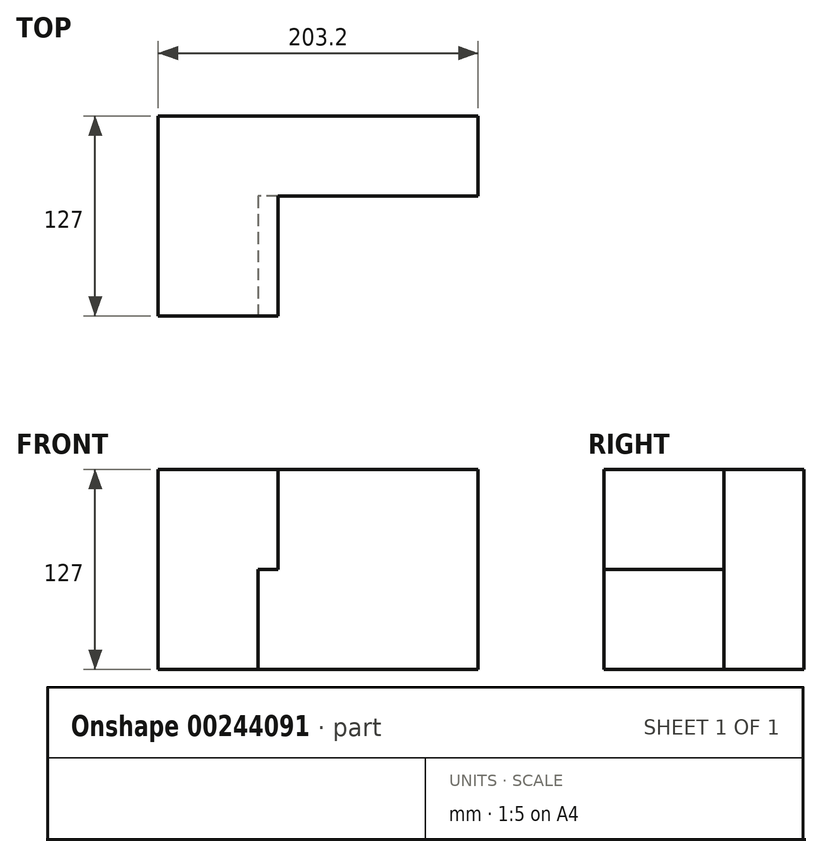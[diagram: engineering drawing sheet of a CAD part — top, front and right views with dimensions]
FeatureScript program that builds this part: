
annotation { "Feature Type Name" : "Feature", "Feature Type Description" : "" }
export const myFeature = defineFeature(function(context is Context, id is Id, definition is map)
    precondition{}
    {
        {
            var Q0;
            Q0=qCreatedBy(makeId("Front.planeOp"),FACE);
            var sketch = newSketch(context, id + "F0", { "sketchPlane" : qUnion([Q0])});
            skLineSegment(sketch, "E0.bottom", {"start": v(101.6, -63.5) * mm, "end": v(-101.6, -63.5) * mm});
            skLineSegment(sketch, "E0.top", {"start": v(101.6, 63.5) * mm, "end": v(-101.6, 63.5) * mm});
            skLineSegment(sketch, "E0.left", {"start": v(101.6, -63.5) * mm, "end": v(101.6, 63.5) * mm});
            skLineSegment(sketch, "E0.right", {"start": v(-101.6, -63.5) * mm, "end": v(-101.6, 63.5) * mm});
            skPoint(sketch, "E0.middle", {"position": v(0, 0) * mm});
            skSolve(sketch);
        }
        {
            var Q0;
            Q0 = qSketchRegion(id + "F0", true);
            extrude(context, id + "F1", {"entities" : qUnion([Q0]), "depth" : 127 * mm});
        }
        {
            var Q0;
            Q0=makeQuery(id+"F1.opExtrude","CAP_FACE",FACE,{"disambiguationData":[OSD([sQuery(id+"F0.wireOp",EDGE,"E0.bottom"),sQuery(id+"F0.wireOp",EDGE,"E0.top"),sQuery(id+"F0.wireOp",EDGE,"E0.left"),sQuery(id+"F0.wireOp",EDGE,"E0.right")])],"isStart":false});
            var sketch = newSketch(context, id + "F2", { "sketchPlane" : qUnion([Q0])});
            skLineSegment(sketch, "E1", {"start": v(-101.6, 63.5) * mm, "end": v(-25.4, 63.5) * mm});
            skLineSegment(sketch, "E2", {"start": v(-101.6, -63.5) * mm, "end": v(-38.1, -63.5) * mm});
            skLineSegment(sketch, "E3", {"start": v(-25.4, 63.5) * mm, "end": v(-25.4, 0) * mm});
            skLineSegment(sketch, "E4", {"start": v(-25.4, 0) * mm, "end": v(-38.1, 0) * mm});
            skLineSegment(sketch, "E5", {"start": v(-38.1, 0) * mm, "end": v(-38.1, -63.5) * mm});
            skLineSegment(sketch, "E6", {"start": v(-101.6, 63.5) * mm, "end": v(-101.6, -63.5) * mm});
            skSolve(sketch);
        }
        {
            var Q0;
            {var subQ3=sQuery(id+"F2.wireOp",EDGE,"E3");Q0=makeQuery(id+"F2.imprint","IMPRINT",FACE,{"disambiguationData":[TD([[makeQuery(id+"F2.imprint","IMPRINT",EDGE,{"derivedFrom":subQ3}),1.0]])]});}
            extrude(context, id + "F3", {"entities" : qUnion([Q0]), "operationType" : NewBodyOperationType.REMOVE, "oppositeDirection" : true, "depth" : 76.2 * mm});
        }
    });
